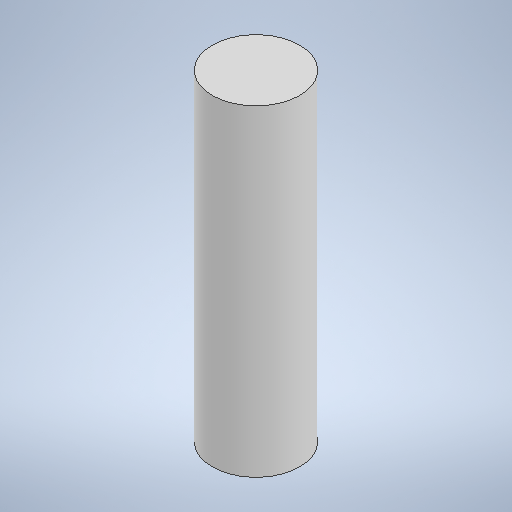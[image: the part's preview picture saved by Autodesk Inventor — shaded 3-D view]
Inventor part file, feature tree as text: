
AUTODESK INVENTOR PART (.ipt)
format: ipt  version: 2025 (Build 290162000, 162)  size: 225,280 bytes
history: native  units: in
note: dims shown in document units (in); Inventor stores cm internally (conversion verified against a paired STEP export)
features: extrude x1, sketch x1
ambient origin geometry x8: Origin, YZ Plane, XZ Plane, XY Plane, X Axis, Y Axis, Z Axis, Center Point
bodies: Solid1 (feature_tree)
feature tree (2):
  extrude  "Extrusion1"  Depth=0.2756in TaperAngle=0.0deg
  sketch  "Sketch1"  dims[d0=0.0748in d1=0.2756in d2=0.0in]
